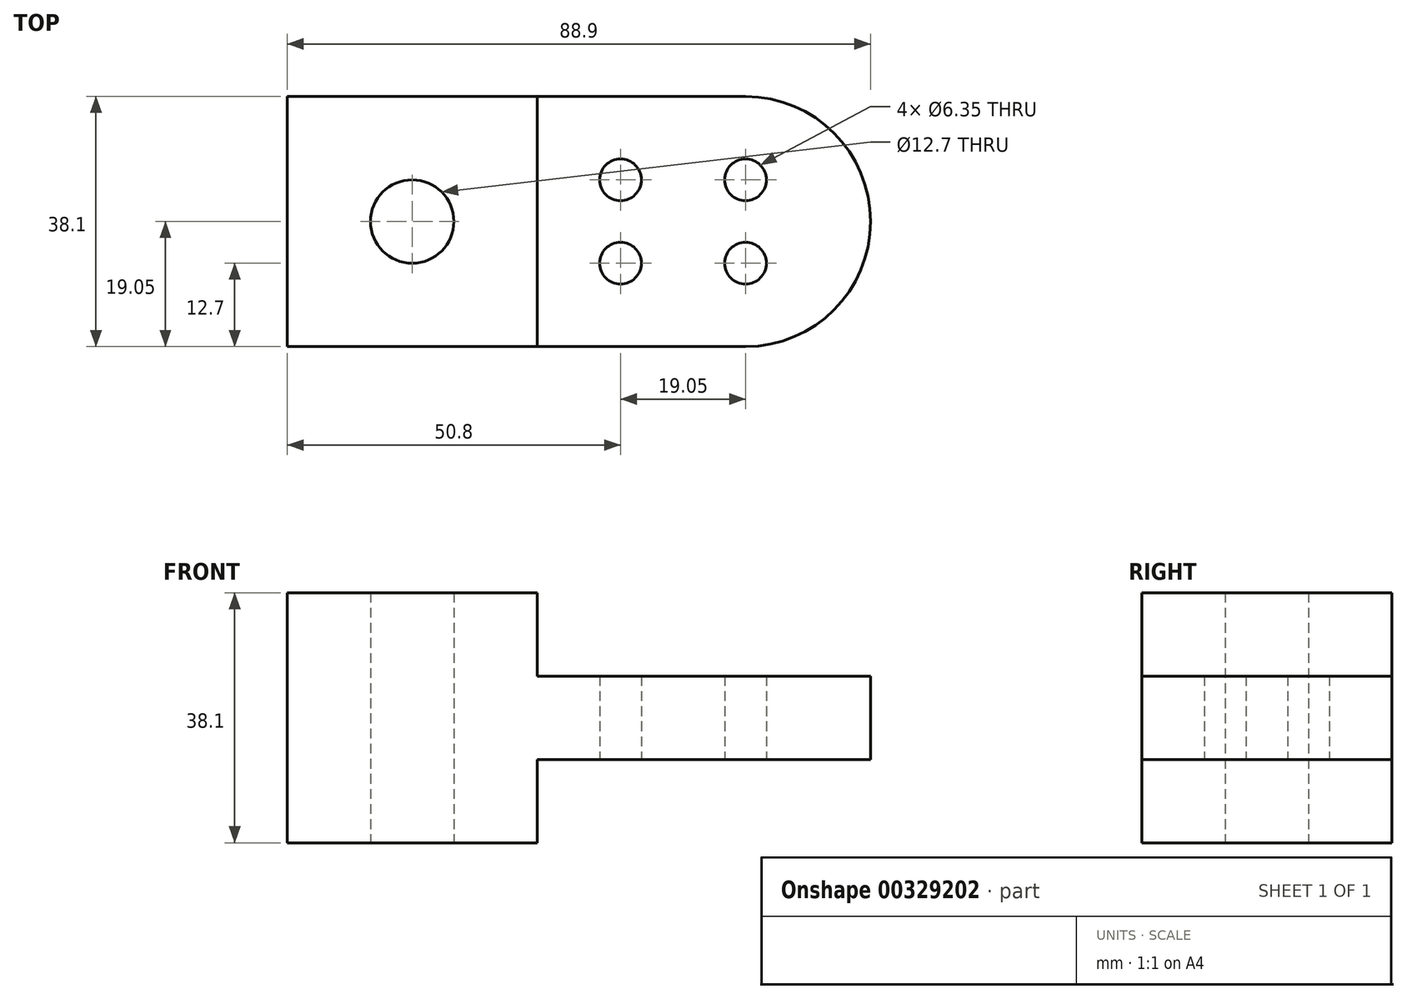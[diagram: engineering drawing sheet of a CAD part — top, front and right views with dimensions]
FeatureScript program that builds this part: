
annotation { "Feature Type Name" : "Feature", "Feature Type Description" : "" }
export const myFeature = defineFeature(function(context is Context, id is Id, definition is map)
    precondition{}
    {
        {
            var Q0;
            Q0=qCreatedBy(makeId("Front.planeOp"),FACE);
            var sketch = newSketch(context, id + "F0", { "sketchPlane" : qUnion([Q0])});
            skLineSegment(sketch, "E0.bottom", {"start": v(0, 0) * mm, "end": v(38.1, 0) * mm});
            skLineSegment(sketch, "E0.top", {"start": v(0, 38.1) * mm, "end": v(38.1, 38.1) * mm});
            skLineSegment(sketch, "E0.left", {"start": v(0, 0) * mm, "end": v(0, 38.1) * mm});
            skLineSegment(sketch, "E0.right", {"start": v(38.1, 0) * mm, "end": v(38.1, 38.1) * mm});
            skLineSegment(sketch, "E1.bottom", {"start": v(38.1, 25.4) * mm, "end": v(88.9, 25.4) * mm});
            skLineSegment(sketch, "E1.top", {"start": v(38.1, 12.7) * mm, "end": v(88.9, 12.7) * mm});
            skLineSegment(sketch, "E1.left", {"start": v(38.1, 25.4) * mm, "end": v(38.1, 12.7) * mm});
            skLineSegment(sketch, "E1.right", {"start": v(88.9, 25.4) * mm, "end": v(88.9, 12.7) * mm});
            skSolve(sketch);
        }
        {
            var Q0;
            Q0 = qSketchRegion(id + "F0", true);
            extrude(context, id + "F1", {"entities" : qUnion([Q0]), "depth" : 38.1 * mm});
        }
        {
            var Q0;
            Q0=makeQuery(id+"F1.opExtrude","SWEPT_FACE",FACE,{"disambiguationData":[OSD([sQuery(id+"F0.wireOp",EDGE,"E1.bottom")])]});
            var sketch = newSketch(context, id + "F2", { "sketchPlane" : qUnion([Q0])});
            skArc(sketch, "E2", {"start": v(69.85, -38.1) * mm, "mid": v(88.9, -19.05) * mm, "end": v(69.85, 0) * mm});
            skPoint(sketch, "E3.orphan", {"position": v(88.9, 0) * mm});
            skPoint(sketch, "E4.orphan", {"position": v(88.9, -38.1) * mm});
            skLineSegment(sketch, "E5.0", {"start": v(69.85, 0) * mm, "end": v(88.9, 0) * mm});
            skLineSegment(sketch, "E6.0", {"start": v(69.85, -38.1) * mm, "end": v(88.9, -38.1) * mm});
            skLineSegment(sketch, "E7.0", {"start": v(88.9, -38.1) * mm, "end": v(88.9, 0) * mm});
            skPoint(sketch, "E8.0.start.orphan", {"position": v(38.1, 0) * mm});
            skPoint(sketch, "E9.0.start.orphan", {"position": v(38.1, -38.1) * mm});
            skSolve(sketch);
        }
        {
            var Q0;
            Q0 = qSketchRegion(id + "F2", true);
            extrude(context, id + "F3", {"entities" : qUnion([Q0]), "operationType" : NewBodyOperationType.REMOVE, "oppositeDirection" : true, "depth" : 25.4 * mm});
        }
        {
            var Q0;
            Q0=qCreatedBy(makeId("Top.planeOp"),FACE);
            var sketch = newSketch(context, id + "F4", { "sketchPlane" : qUnion([Q0])});
            skLineSegment(sketch, "E10", {"start": v(19.05, 34.76) * mm, "end": v(19.05, -54.63) * mm, "construction": true});
            skLineSegment(sketch, "E11", {"start": v(-30.66, -19.05) * mm, "end": v(106.8, -19.05) * mm, "construction": true});
            skCircle(sketch, "E12", {"center": v(19.05, -19.05) * mm, "radius": 6.35 * mm});
            skPoint(sketch, "E12.centerSnap0", {"position": v(38.07, -19.05) * mm});
            skCircle(sketch, "E13", {"center": v(50.8, -12.7) * mm, "radius": 3.18 * mm});
            skCircle(sketch, "E14", {"center": v(50.8, -25.4) * mm, "radius": 3.18 * mm});
            skCircle(sketch, "E15", {"center": v(69.85, -25.4) * mm, "radius": 3.18 * mm});
            skCircle(sketch, "E16", {"center": v(69.85, -12.7) * mm, "radius": 3.18 * mm});
            skPoint(sketch, "E17.orphan", {"position": v(0, 0) * mm});
            skPoint(sketch, "E18.orphan", {"position": v(0, -38.1) * mm});
            skPoint(sketch, "E19.orphan", {"position": v(38.1, -38.1) * mm});
            skPoint(sketch, "E20.0.3.end.orphan", {"position": v(38.1, 0) * mm});
            skSolve(sketch);
        }
        {
            var Q0;
            Q0 = qSketchRegion(id + "F4", true);
            extrude(context, id + "F5", {"entities" : qUnion([Q0]), "operationType" : NewBodyOperationType.REMOVE, "endBound" : BoundingType.THROUGH_ALL, "depth" : 25.4 * mm});
        }
    });
